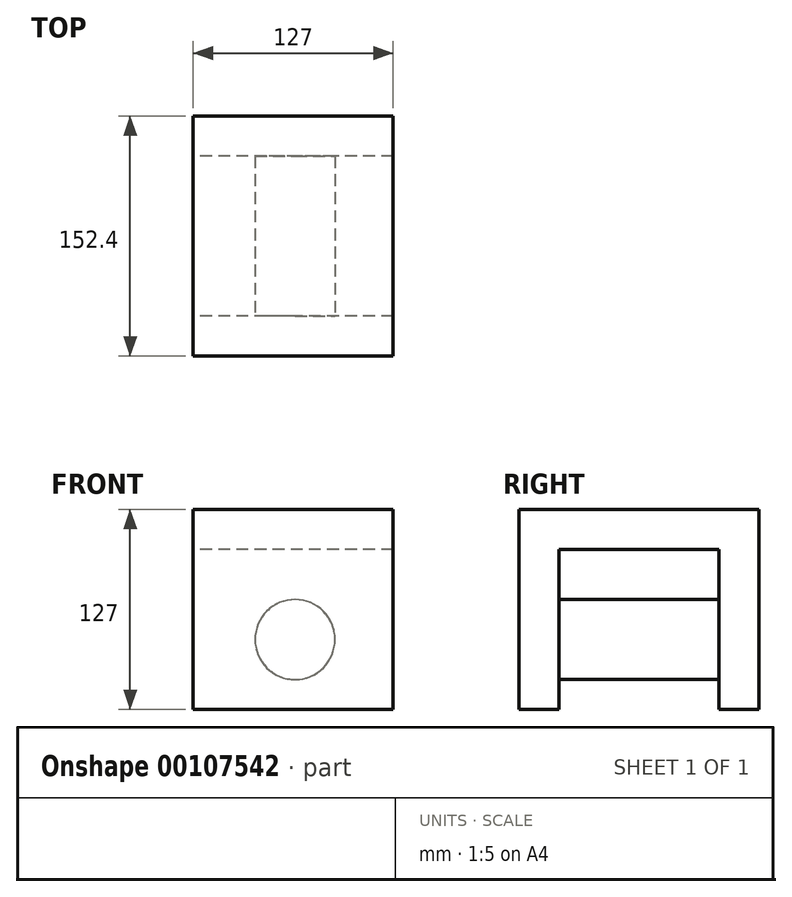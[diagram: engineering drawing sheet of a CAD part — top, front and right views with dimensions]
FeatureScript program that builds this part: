
annotation { "Feature Type Name" : "Feature", "Feature Type Description" : "" }
export const myFeature = defineFeature(function(context is Context, id is Id, definition is map)
    precondition{}
    {
        {
            var Q0;
            Q0=qCreatedBy(makeId("Right.planeOp"),FACE);
            var sketch = newSketch(context, id + "F0", { "sketchPlane" : qUnion([Q0])});
            skLineSegment(sketch, "E0", {"start": v(-88.65, 56.26) * mm, "end": v(63.75, 56.26) * mm});
            skLineSegment(sketch, "E1", {"start": v(63.75, 56.26) * mm, "end": v(63.75, -70.74) * mm});
            skLineSegment(sketch, "E2", {"start": v(38.35, -70.74) * mm, "end": v(38.35, 30.86) * mm});
            skLineSegment(sketch, "E3", {"start": v(38.35, 30.86) * mm, "end": v(-63.25, 30.86) * mm});
            skLineSegment(sketch, "E4", {"start": v(-63.25, 30.86) * mm, "end": v(-63.25, -70.74) * mm});
            skLineSegment(sketch, "E5", {"start": v(-88.65, 56.26) * mm, "end": v(-88.65, -70.74) * mm});
            skLineSegment(sketch, "E6", {"start": v(-63.25, -70.74) * mm, "end": v(-88.65, -70.74) * mm});
            skLineSegment(sketch, "E7", {"start": v(38.35, -70.74) * mm, "end": v(63.75, -70.74) * mm});
            skSolve(sketch);
        }
        {
            var Q0;
            Q0=makeQuery(id+"F0.imprint","IMPRINT",FACE,{"disambiguationData":[TD([[makeQuery(id+"F0.imprint","IMPRINT",EDGE,{"derivedFrom":sQuery(id+"F0.wireOp",EDGE,"E0")}),-1.0]])]});
            extrude(context, id + "F1", {"entities" : qUnion([Q0]), "depth" : 127 * mm});
        }
        {
            var Q0;
            Q0=makeQuery(id+"F1.opExtrude","SWEPT_FACE",FACE,{"disambiguationData":[OSD([sQuery(id+"F0.wireOp",EDGE,"E5")])]});
            var sketch = newSketch(context, id + "F2", { "sketchPlane" : qUnion([Q0])});
            skCircle(sketch, "E8", {"center": v(64.7, -26.33) * mm, "radius": 25.4 * mm});
            skSolve(sketch);
        }
        {
            var Q0;
            Q0=makeQuery(id+"F2.imprint","IMPRINT",FACE,{"disambiguationData":[TD([[makeQuery(id+"F2.imprint","IMPRINT",EDGE,{"derivedFrom":sQuery(id+"F2.wireOp",EDGE,"E8")}),1.0]])]});
            extrude(context, id + "F3", {"entities" : qUnion([Q0]), "operationType" : NewBodyOperationType.ADD, "oppositeDirection" : true, "depth" : 152.4 * mm});
        }
    });
